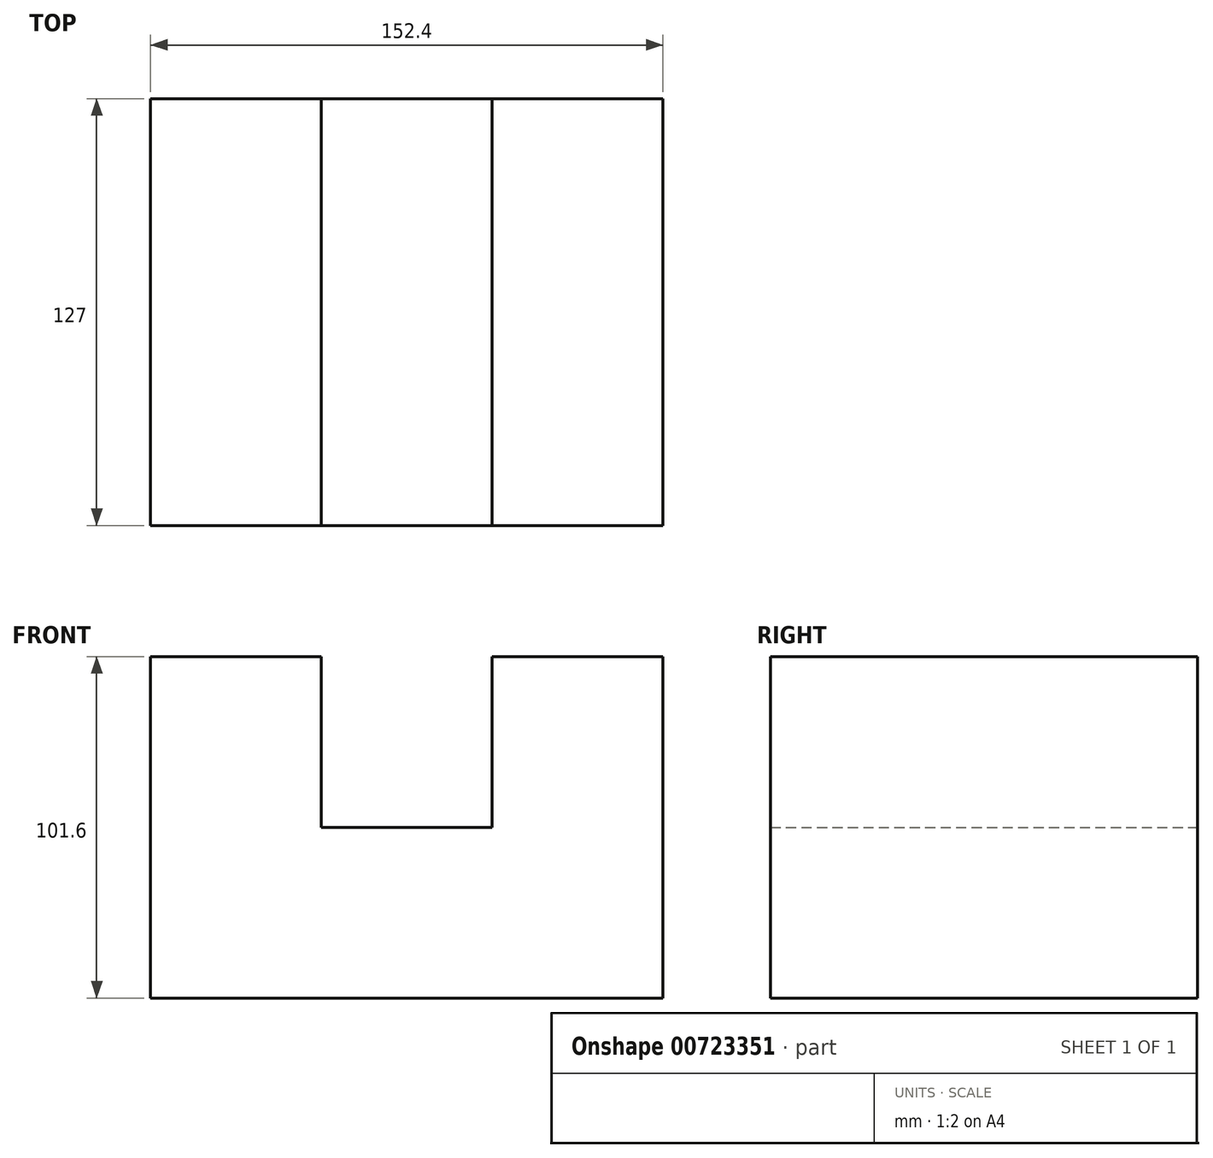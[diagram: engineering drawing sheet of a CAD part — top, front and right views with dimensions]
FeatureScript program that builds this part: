
annotation { "Feature Type Name" : "Feature", "Feature Type Description" : "" }
export const myFeature = defineFeature(function(context is Context, id is Id, definition is map)
    precondition{}
    {
        {
            var Q0;
            Q0=qCreatedBy(makeId("Front.planeOp"),FACE);
            var sketch = newSketch(context, id + "F0", { "sketchPlane" : qUnion([Q0])});
            skLineSegment(sketch, "E0", {"start": v(-89.93, 70.6) * mm, "end": v(-89.93, -31) * mm});
            skLineSegment(sketch, "E1", {"start": v(-89.93, -31) * mm, "end": v(62.47, -31) * mm});
            skLineSegment(sketch, "E2", {"start": v(62.47, -31) * mm, "end": v(62.47, 70.6) * mm});
            skLineSegment(sketch, "E3", {"start": v(62.47, 70.6) * mm, "end": v(11.67, 70.6) * mm});
            skLineSegment(sketch, "E4", {"start": v(11.67, 70.6) * mm, "end": v(11.67, 19.8) * mm});
            skLineSegment(sketch, "E5", {"start": v(11.67, 19.8) * mm, "end": v(-39.13, 19.8) * mm});
            skLineSegment(sketch, "E6", {"start": v(-39.13, 19.8) * mm, "end": v(-39.13, 70.6) * mm});
            skLineSegment(sketch, "E7", {"start": v(-39.13, 70.6) * mm, "end": v(-89.93, 70.6) * mm});
            skSolve(sketch);
        }
        {
            var Q0;
            Q0=makeQuery(id+"F0.imprint","IMPRINT",FACE,{"disambiguationData":[TD([[makeQuery(id+"F0.imprint","IMPRINT",EDGE,{"derivedFrom":sQuery(id+"F0.wireOp",EDGE,"E0")}),1.0]])]});
            extrude(context, id + "F1", {"entities" : qUnion([Q0]), "depth" : 127 * mm, "offsetDistance" : 25.4 * mm});
        }
    });
